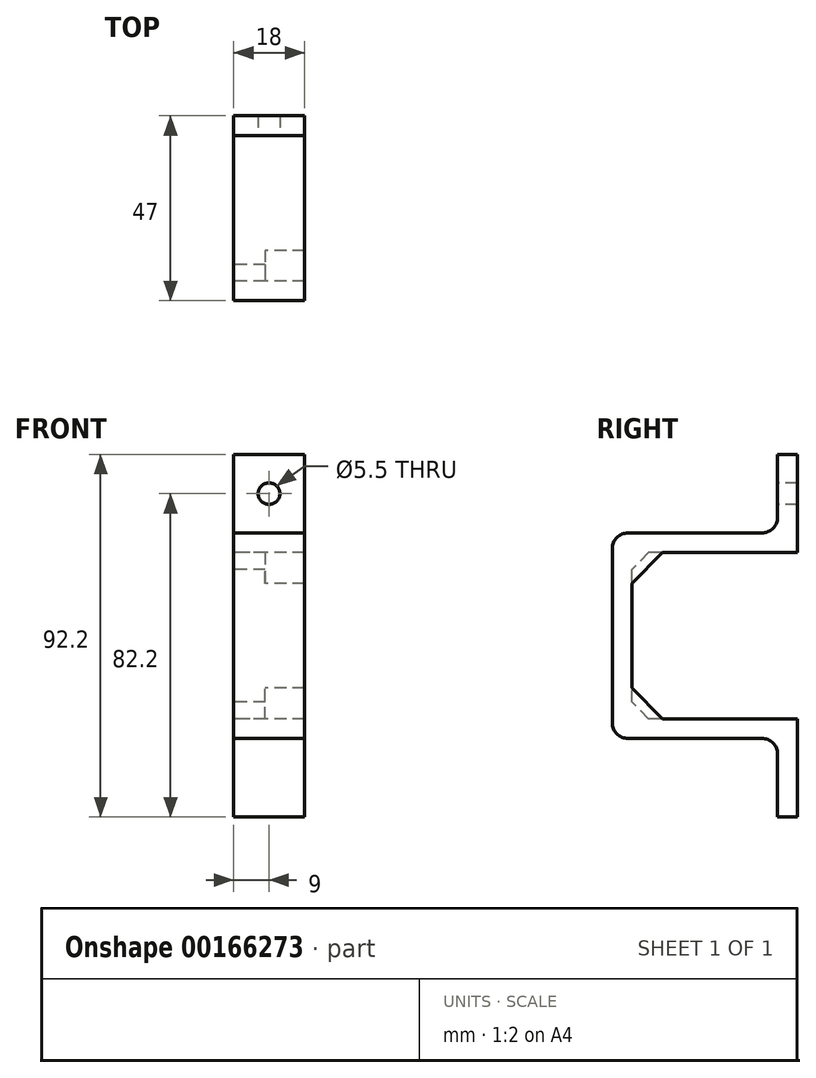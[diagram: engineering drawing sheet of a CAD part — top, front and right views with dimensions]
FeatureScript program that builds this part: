
annotation { "Feature Type Name" : "Feature", "Feature Type Description" : "" }
export const myFeature = defineFeature(function(context is Context, id is Id, definition is map)
    precondition{}
    {
        {
            var Q0;
            Q0=qCreatedBy(makeId("Right.planeOp"),FACE);
            var sketch = newSketch(context, id + "F0", { "sketchPlane" : qUnion([Q0])});
            skLineSegment(sketch, "E0", {"start": v(47, 0) * mm, "end": v(0, 0) * mm, "construction": true});
            skLineSegment(sketch, "E1", {"start": v(0, 0) * mm, "end": v(0, 26.1) * mm});
            skLineSegment(sketch, "E2", {"start": v(42, 26.1) * mm, "end": v(42, 46.1) * mm});
            skLineSegment(sketch, "E3", {"start": v(42, 46.1) * mm, "end": v(47, 46.1) * mm});
            skLineSegment(sketch, "E4", {"start": v(47, 46.1) * mm, "end": v(47, 21.1) * mm});
            skLineSegment(sketch, "E5", {"start": v(47, 21.1) * mm, "end": v(9.24, 21.1) * mm});
            skLineSegment(sketch, "E6", {"start": v(9.24, 21.1) * mm, "end": v(5, 16.86) * mm});
            skLineSegment(sketch, "E7", {"start": v(5, 16.86) * mm, "end": v(5, 0) * mm});
            skLineSegment(sketch, "E8", {"start": v(0, 26.1) * mm, "end": v(42, 26.1) * mm});
            skLineSegment(sketch, "E9", {"start": v(5, 16.86) * mm, "end": v(9.24, 16.86) * mm, "construction": true});
            skLineSegment(sketch, "E10.MirrorCS", {"start": v(42, -46.1) * mm, "end": v(47, -46.1) * mm});
            skLineSegment(sketch, "E11.MirrorCS", {"start": v(9.24, -21.1) * mm, "end": v(5, -16.86) * mm});
            skLineSegment(sketch, "E12.MirrorCS", {"start": v(5, -16.86) * mm, "end": v(9.24, -16.86) * mm, "construction": true});
            skLineSegment(sketch, "E13.MirrorCS", {"start": v(0, -26.1) * mm, "end": v(42, -26.1) * mm});
            skLineSegment(sketch, "E14.MirrorCS", {"start": v(0, 0) * mm, "end": v(0, -26.1) * mm});
            skLineSegment(sketch, "E15.MirrorCS", {"start": v(5, -16.86) * mm, "end": v(5, 0) * mm});
            skLineSegment(sketch, "E16.MirrorCS", {"start": v(47, -46.1) * mm, "end": v(47, -21.1) * mm});
            skLineSegment(sketch, "E17.MirrorCS", {"start": v(47, -21.1) * mm, "end": v(9.24, -21.1) * mm});
            skLineSegment(sketch, "E18.MirrorCS", {"start": v(42, -26.1) * mm, "end": v(42, -46.1) * mm});
            skSolve(sketch);
        }
        {
            var Q0;
            Q0=makeQuery(id+"F0.imprint","IMPRINT",FACE,{"disambiguationData":[TD([[makeQuery(id+"F0.imprint","IMPRINT",EDGE,{"derivedFrom":sQuery(id+"F0.wireOp",EDGE,"E1")}),-1.0]])]});
            extrude(context, id + "F1", {"entities" : qUnion([Q0]), "depth" : 8 * mm});
        }
        {
            var Q0;
            Q0=makeQuery(id+"F1.opExtrude","CAP_FACE",FACE,{"disambiguationData":[OSD([sQuery(id+"F0.wireOp",EDGE,"E1"),sQuery(id+"F0.wireOp",EDGE,"E2"),sQuery(id+"F0.wireOp",EDGE,"E3"),sQuery(id+"F0.wireOp",EDGE,"E4"),sQuery(id+"F0.wireOp",EDGE,"E5"),sQuery(id+"F0.wireOp",EDGE,"E6"),sQuery(id+"F0.wireOp",EDGE,"E7"),sQuery(id+"F0.wireOp",EDGE,"E8"),sQuery(id+"F0.wireOp",EDGE,"E10.MirrorCS"),sQuery(id+"F0.wireOp",EDGE,"E11.MirrorCS"),sQuery(id+"F0.wireOp",EDGE,"E13.MirrorCS"),sQuery(id+"F0.wireOp",EDGE,"E14.MirrorCS"),sQuery(id+"F0.wireOp",EDGE,"E15.MirrorCS"),sQuery(id+"F0.wireOp",EDGE,"E16.MirrorCS"),sQuery(id+"F0.wireOp",EDGE,"E17.MirrorCS"),sQuery(id+"F0.wireOp",EDGE,"E18.MirrorCS")])],"isStart":false});
            var sketch = newSketch(context, id + "F2", { "sketchPlane" : qUnion([Q0])});
            skLineSegment(sketch, "E19.0", {"start": v(0, -26.1) * mm, "end": v(42, -26.1) * mm});
            skLineSegment(sketch, "E19.2", {"start": v(47, -46.1) * mm, "end": v(47, -21.1) * mm});
            skLineSegment(sketch, "E19.4", {"start": v(42, 26.1) * mm, "end": v(42, 46.1) * mm});
            skLineSegment(sketch, "E20", {"start": v(0, -26.1) * mm, "end": v(0, 26.1) * mm});
            skLineSegment(sketch, "E21", {"start": v(0, 26.1) * mm, "end": v(42, 26.1) * mm});
            skLineSegment(sketch, "E22", {"start": v(42, 46.1) * mm, "end": v(47, 46.1) * mm});
            skLineSegment(sketch, "E23", {"start": v(47, 46.1) * mm, "end": v(47, 21.1) * mm});
            skLineSegment(sketch, "E24", {"start": v(47, 21.1) * mm, "end": v(12.78, 21.1) * mm});
            skLineSegment(sketch, "E25", {"start": v(12.78, 21.1) * mm, "end": v(5, 13.32) * mm});
            skLineSegment(sketch, "E26", {"start": v(5, 13.32) * mm, "end": v(5, 0) * mm});
            skLineSegment(sketch, "E27", {"start": v(5, 0) * mm, "end": v(0, 0) * mm, "construction": true});
            skLineSegment(sketch, "E28", {"start": v(5, 13.32) * mm, "end": v(12.78, 13.32) * mm, "construction": true});
            skLineSegment(sketch, "E29.MirrorCS", {"start": v(12.78, -21.1) * mm, "end": v(5, -13.32) * mm});
            skLineSegment(sketch, "E30.MirrorCS", {"start": v(5, -13.32) * mm, "end": v(5, 0) * mm});
            skLineSegment(sketch, "E31.MirrorCS", {"start": v(47, -21.1) * mm, "end": v(12.78, -21.1) * mm});
            skLineSegment(sketch, "E32.MirrorCS", {"start": v(42, -26.1) * mm, "end": v(42, -46.1) * mm});
            skLineSegment(sketch, "E33.MirrorCS", {"start": v(42, -46.1) * mm, "end": v(47, -46.1) * mm});
            skSolve(sketch);
        }
        {
            var Q0;
            {var subQ0=sQuery(id+"F2.wireOp",EDGE,"E25");Q0=makeQuery(id+"F2.imprint","IMPRINT",FACE,{"disambiguationData":[TD([[makeQuery(id+"F2.imprint","IMPRINT",EDGE,{"derivedFrom":subQ0}),-1.0]])]});}
            var Q1;
            Q1=makeQuery(id+"F2.imprint","IMPRINT",FACE,{"disambiguationData":[TD([[makeQuery(id+"F2.imprint","IMPRINT",EDGE,{"derivedFrom":sQuery(id+"F2.wireOp",EDGE,"E19.0")}),1.0]])]});
            var Q2;
            {var subQ0=sQuery(id+"F2.wireOp",EDGE,"E29.MirrorCS");Q2=makeQuery(id+"F2.imprint","IMPRINT",FACE,{"disambiguationData":[TD([[makeQuery(id+"F2.imprint","IMPRINT",EDGE,{"derivedFrom":subQ0}),1.0]])]});}
            extrude(context, id + "F3", {"entities" : qUnion([Q0, Q1, Q2]), "operationType" : NewBodyOperationType.ADD, "depth" : 10 * mm});
        }
        {
            var Q0;
            Q0=makeQuery(id+"F3.boolean.opBoolean","MERGE",FACE,{"derivedFrom":[makeQuery(id+"F1.opExtrude","SWEPT_FACE",FACE,{"disambiguationData":[OSD([sQuery(id+"F0.wireOp",EDGE,"E2")])]}),makeQuery(id+"F3.opExtrude","SWEPT_FACE",FACE,{"disambiguationData":[OSD([sQuery(id+"F2.wireOp",EDGE,"E19.4")])]})]});
            var sketch = newSketch(context, id + "F4", { "sketchPlane" : qUnion([Q0])});
            skCircle(sketch, "E34", {"center": v(9, 36.1) * mm, "radius": 2.75 * mm});
            skPoint(sketch, "E34.centerSnap0", {"position": v(9, 46.1) * mm});
            skPoint(sketch, "E34.centerSnap1", {"position": v(18, 36.1) * mm});
            skLineSegment(sketch, "E35.0", {"start": v(18, -26.1) * mm, "end": v(18, 26.1) * mm, "construction": true});
            skLineSegment(sketch, "E36", {"start": v(18, 0) * mm, "end": v(9, 0) * mm, "construction": true});
            skPoint(sketch, "E36.endSnap0", {"position": v(18, 0) * mm});
            skCircle(sketch, "E37.MirrorC", {"center": v(9, -36.1) * mm, "radius": 2.75 * mm});
            skSolve(sketch);
        }
        {
            var Q0;
            Q0=makeQuery(id+"F4.imprint","IMPRINT",FACE,{"disambiguationData":[TD([[makeQuery(id+"F4.imprint","IMPRINT",EDGE,{"derivedFrom":sQuery(id+"F4.wireOp",EDGE,"E34")}),1.0]])]});
            var Q1;
            Q1=makeQuery(id+"F4.imprint","IMPRINT",FACE,{"disambiguationData":[TD([[makeQuery(id+"F4.imprint","IMPRINT",EDGE,{"derivedFrom":sQuery(id+"F4.wireOp",EDGE,"E37.MirrorC")}),-1.0]])]});
            extrude(context, id + "F5", {"entities" : qUnion([Q0, Q1]), "operationType" : NewBodyOperationType.REMOVE, "oppositeDirection" : true, "depth" : 25 * mm});
        }
        {
            var Q0;
            Q0=makeQuery(id+"F3.boolean.opBoolean","MERGE",EDGE,{"derivedFrom":[makeQuery(id+"F1.opExtrude","SWEPT_EDGE",EDGE,{"disambiguationData":[OSD([sQuery(id+"F0.wireOp",EDGE,"E1"),sQuery(id+"F0.wireOp",EDGE,"E8")])]}),makeQuery(id+"F3.opExtrude","SWEPT_EDGE",EDGE,{"disambiguationData":[OSD([sQuery(id+"F2.wireOp",EDGE,"E20"),sQuery(id+"F2.wireOp",EDGE,"E21")])]})]});
            var Q1;
            Q1=makeQuery(id+"F3.boolean.opBoolean","MERGE",EDGE,{"derivedFrom":[makeQuery(id+"F1.opExtrude","SWEPT_EDGE",EDGE,{"disambiguationData":[OSD([sQuery(id+"F0.wireOp",EDGE,"E13.MirrorCS"),sQuery(id+"F0.wireOp",EDGE,"E14.MirrorCS")])]}),makeQuery(id+"F3.opExtrude","SWEPT_EDGE",EDGE,{"disambiguationData":[OSD([sQuery(id+"F2.wireOp",EDGE,"E19.0"),sQuery(id+"F2.wireOp",EDGE,"E20")])]})]});
            var Q2;
            Q2=makeQuery(id+"F3.boolean.opBoolean","MERGE",EDGE,{"derivedFrom":[makeQuery(id+"F1.opExtrude","SWEPT_EDGE",EDGE,{"disambiguationData":[OSD([sQuery(id+"F0.wireOp",EDGE,"E13.MirrorCS"),sQuery(id+"F0.wireOp",EDGE,"E18.MirrorCS")])]}),makeQuery(id+"F3.opExtrude","SWEPT_EDGE",EDGE,{"disambiguationData":[OSD([sQuery(id+"F2.wireOp",EDGE,"E19.0"),sQuery(id+"F2.wireOp",EDGE,"E32.MirrorCS")])]})]});
            var Q3;
            Q3=makeQuery(id+"F3.boolean.opBoolean","MERGE",EDGE,{"derivedFrom":[makeQuery(id+"F1.opExtrude","SWEPT_EDGE",EDGE,{"disambiguationData":[OSD([sQuery(id+"F0.wireOp",EDGE,"E2"),sQuery(id+"F0.wireOp",EDGE,"E8")])]}),makeQuery(id+"F3.opExtrude","SWEPT_EDGE",EDGE,{"disambiguationData":[OSD([sQuery(id+"F2.wireOp",EDGE,"E19.4"),sQuery(id+"F2.wireOp",EDGE,"E21")])]})]});
            fillet(context, id + "F6", {"entities" : qUnion([Q0, Q1, Q2, Q3]), "radius" : 4 * mm, "tangentPropagation" : true, "allowEdgeOverflow" : false});
        }
    });
